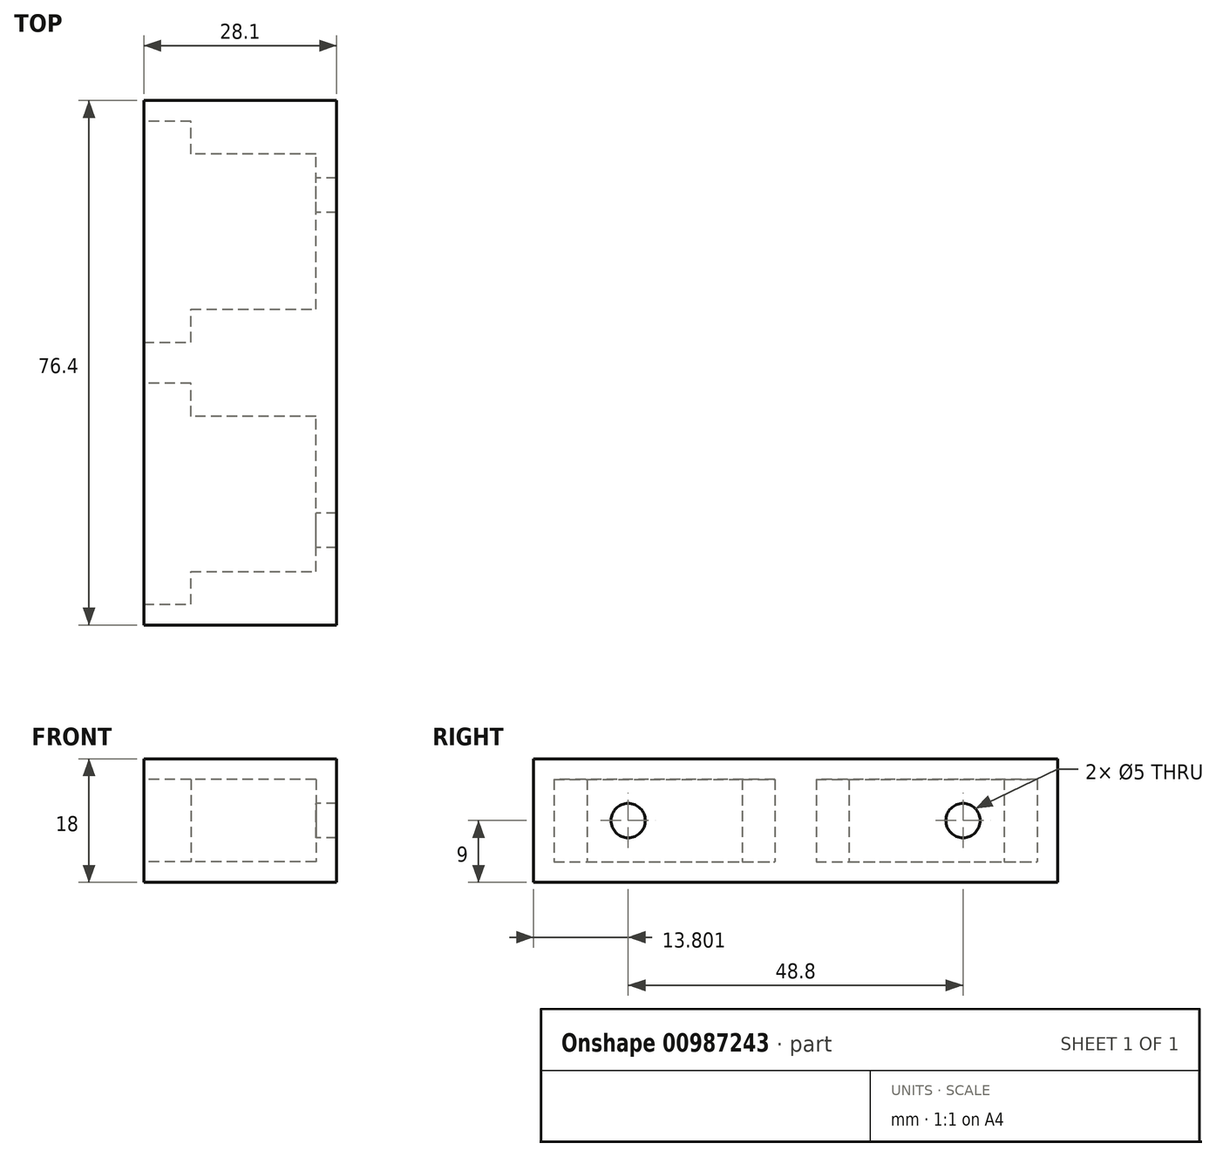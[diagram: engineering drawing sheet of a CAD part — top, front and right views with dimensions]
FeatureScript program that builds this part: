
annotation { "Feature Type Name" : "Feature", "Feature Type Description" : "" }
export const myFeature = defineFeature(function(context is Context, id is Id, definition is map)
    precondition{}
    {
        {
            assignVariable(context, id + "F0", {"name" : "ServoF", "anyValue" : 12});
        }
        {
            var Q0;
            Q0=qCreatedBy(makeId("Top.planeOp"),FACE);
            var sketch = newSketch(context, id + "F1", { "sketchPlane" : qUnion([Q0])});
            skLineSegment(sketch, "E0", {"start": v(-63.12, 39.48) * mm, "end": v(-35.02, 39.48) * mm});
            skLineSegment(sketch, "E1", {"start": v(-35.02, 39.48) * mm, "end": v(-35.02, -36.92) * mm});
            skLineSegment(sketch, "E2", {"start": v(-35.02, -36.92) * mm, "end": v(-63.12, -36.92) * mm});
            skLineSegment(sketch, "E3", {"start": v(-63.12, -36.92) * mm, "end": v(-63.12, -33.92) * mm});
            skLineSegment(sketch, "E4", {"start": v(-63.12, -33.92) * mm, "end": v(-56.27, -33.92) * mm});
            skLineSegment(sketch, "E5", {"start": v(-56.27, -33.92) * mm, "end": v(-56.27, -29.12) * mm});
            skLineSegment(sketch, "E6", {"start": v(-56.27, -29.12) * mm, "end": v(-38.02, -29.12) * mm});
            skLineSegment(sketch, "E7", {"start": v(-38.02, -29.12) * mm, "end": v(-38.02, -6.52) * mm});
            skLineSegment(sketch, "E8", {"start": v(-38.02, -6.52) * mm, "end": v(-56.27, -6.52) * mm});
            skLineSegment(sketch, "E9", {"start": v(-56.27, -6.52) * mm, "end": v(-56.27, -1.72) * mm});
            skLineSegment(sketch, "E10", {"start": v(-56.27, -1.72) * mm, "end": v(-63.12, -1.72) * mm});
            skLineSegment(sketch, "E11", {"start": v(-63.12, -1.72) * mm, "end": v(-63.12, 4.28) * mm});
            skLineSegment(sketch, "E12", {"start": v(-63.12, 4.28) * mm, "end": v(-56.27, 4.28) * mm});
            skLineSegment(sketch, "E13", {"start": v(-56.27, 4.28) * mm, "end": v(-56.27, 9.08) * mm});
            skLineSegment(sketch, "E14", {"start": v(-56.27, 9.08) * mm, "end": v(-38.02, 9.08) * mm});
            skLineSegment(sketch, "E15", {"start": v(-38.02, 9.08) * mm, "end": v(-38.02, 31.68) * mm});
            skLineSegment(sketch, "E16", {"start": v(-38.02, 31.68) * mm, "end": v(-56.27, 31.68) * mm});
            skLineSegment(sketch, "E17", {"start": v(-56.27, 31.68) * mm, "end": v(-56.27, 36.48) * mm});
            skLineSegment(sketch, "E18", {"start": v(-56.27, 36.48) * mm, "end": v(-63.12, 36.48) * mm});
            skLineSegment(sketch, "E19", {"start": v(-63.12, 36.48) * mm, "end": v(-63.12, 39.48) * mm});
            skSolve(sketch);
        }
        {
            var Q0;
            Q0=qSketchRegion(id+"F1",true);
            extrude(context, id + "F2", {"entities" : qUnion([Q0]), "depth" : (getVariable(context, 'ServoF')) * mm, "offsetDistance" : 25 * mm});
        }
        {
            var Q0;
            Q0=makeQuery(id+"F2.opExtrude","CAP_FACE",FACE,{"disambiguationData":[OSD([sQuery(id+"F1.wireOp",EDGE,"E0"),sQuery(id+"F1.wireOp",EDGE,"E1"),sQuery(id+"F1.wireOp",EDGE,"E2"),sQuery(id+"F1.wireOp",EDGE,"E3"),sQuery(id+"F1.wireOp",EDGE,"E4"),sQuery(id+"F1.wireOp",EDGE,"E5"),sQuery(id+"F1.wireOp",EDGE,"E6"),sQuery(id+"F1.wireOp",EDGE,"E7"),sQuery(id+"F1.wireOp",EDGE,"E8"),sQuery(id+"F1.wireOp",EDGE,"E9"),sQuery(id+"F1.wireOp",EDGE,"E10"),sQuery(id+"F1.wireOp",EDGE,"E11"),sQuery(id+"F1.wireOp",EDGE,"E12"),sQuery(id+"F1.wireOp",EDGE,"E13"),sQuery(id+"F1.wireOp",EDGE,"E14"),sQuery(id+"F1.wireOp",EDGE,"E15"),sQuery(id+"F1.wireOp",EDGE,"E16"),sQuery(id+"F1.wireOp",EDGE,"E17"),sQuery(id+"F1.wireOp",EDGE,"E18"),sQuery(id+"F1.wireOp",EDGE,"E19")])],"isStart":false});
            var sketch = newSketch(context, id + "F3", { "sketchPlane" : qUnion([Q0])});
            skLineSegment(sketch, "E20.bottom", {"start": v(-63.12, -36.92) * mm, "end": v(-35.02, -36.92) * mm});
            skLineSegment(sketch, "E20.top", {"start": v(-63.12, 39.48) * mm, "end": v(-35.02, 39.48) * mm});
            skLineSegment(sketch, "E20.left", {"start": v(-63.12, 39.48) * mm, "end": v(-63.12, -36.92) * mm});
            skLineSegment(sketch, "E20.right", {"start": v(-35.02, 39.48) * mm, "end": v(-35.02, -36.92) * mm});
            skSolve(sketch);
        }
        {
            var Q0;
            Q0=makeQuery(id+"F2.opExtrude","CAP_FACE",FACE,{"disambiguationData":[OSD([sQuery(id+"F1.wireOp",EDGE,"E0"),sQuery(id+"F1.wireOp",EDGE,"E1"),sQuery(id+"F1.wireOp",EDGE,"E2"),sQuery(id+"F1.wireOp",EDGE,"E3"),sQuery(id+"F1.wireOp",EDGE,"E4"),sQuery(id+"F1.wireOp",EDGE,"E5"),sQuery(id+"F1.wireOp",EDGE,"E6"),sQuery(id+"F1.wireOp",EDGE,"E7"),sQuery(id+"F1.wireOp",EDGE,"E8"),sQuery(id+"F1.wireOp",EDGE,"E9"),sQuery(id+"F1.wireOp",EDGE,"E10"),sQuery(id+"F1.wireOp",EDGE,"E11"),sQuery(id+"F1.wireOp",EDGE,"E12"),sQuery(id+"F1.wireOp",EDGE,"E13"),sQuery(id+"F1.wireOp",EDGE,"E14"),sQuery(id+"F1.wireOp",EDGE,"E15"),sQuery(id+"F1.wireOp",EDGE,"E16"),sQuery(id+"F1.wireOp",EDGE,"E17"),sQuery(id+"F1.wireOp",EDGE,"E18"),sQuery(id+"F1.wireOp",EDGE,"E19")])],"isStart":true});
            var sketch = newSketch(context, id + "F4", { "sketchPlane" : qUnion([Q0])});
            skLineSegment(sketch, "E21.bottom", {"start": v(-63.12, -39.48) * mm, "end": v(-35.02, -39.48) * mm});
            skLineSegment(sketch, "E21.top", {"start": v(-63.12, 36.92) * mm, "end": v(-35.02, 36.92) * mm});
            skLineSegment(sketch, "E21.left", {"start": v(-63.12, 36.92) * mm, "end": v(-63.12, -39.48) * mm});
            skLineSegment(sketch, "E21.right", {"start": v(-35.02, 36.92) * mm, "end": v(-35.02, -39.48) * mm});
            skSolve(sketch);
        }
        {
            var Q0;
            Q0=makeQuery(id+"F2.opExtrude","SWEPT_FACE",FACE,{"disambiguationData":[OSD([sQuery(id+"F1.wireOp",EDGE,"E15")])]});
            var sketch = newSketch(context, id + "F5", { "sketchPlane" : qUnion([Q0])});
            skCircle(sketch, "E22", {"center": v(-25.68, 6) * mm, "radius": 2.5 * mm});
            skCircle(sketch, "E23", {"center": v(0, 0) * mm, "radius": 2.5 * mm});
            skSolve(sketch);
        }
        {
            var Q0;
            Q0=makeQuery(id+"F2.opExtrude","SWEPT_FACE",FACE,{"disambiguationData":[OSD([sQuery(id+"F1.wireOp",EDGE,"E7")])]});
            var sketch = newSketch(context, id + "F6", { "sketchPlane" : qUnion([Q0])});
            skCircle(sketch, "E24", {"center": v(23.12, 6) * mm, "radius": 2.5 * mm});
            skSolve(sketch);
        }
        {
            var Q0;
            Q0=qSketchRegion(id+"F3",true);
            extrude(context, id + "F7", {"entities" : qUnion([Q0]), "operationType" : NewBodyOperationType.ADD, "depth" : 3 * mm, "offsetDistance" : 25 * mm});
        }
        {
            var Q0;
            Q0=qSketchRegion(id+"F4",true);
            extrude(context, id + "F8", {"entities" : qUnion([Q0]), "operationType" : NewBodyOperationType.ADD, "depth" : 3 * mm, "offsetDistance" : 25 * mm});
        }
        {
            var Q0;
            Q0=sQuery(id+"F5.wireOp",VERTEX,"E22.center");
            var Q1;
            Q1=makeQuery(id+"F2.opExtrude","SWEPT_BODY",BODY,{"disambiguationData":[OSD([sQuery(id+"F1.wireOp",EDGE,"E0"),sQuery(id+"F1.wireOp",EDGE,"E1"),sQuery(id+"F1.wireOp",EDGE,"E2"),sQuery(id+"F1.wireOp",EDGE,"E3"),sQuery(id+"F1.wireOp",EDGE,"E4"),sQuery(id+"F1.wireOp",EDGE,"E5"),sQuery(id+"F1.wireOp",EDGE,"E6"),sQuery(id+"F1.wireOp",EDGE,"E7"),sQuery(id+"F1.wireOp",EDGE,"E8"),sQuery(id+"F1.wireOp",EDGE,"E9"),sQuery(id+"F1.wireOp",EDGE,"E10"),sQuery(id+"F1.wireOp",EDGE,"E11"),sQuery(id+"F1.wireOp",EDGE,"E12"),sQuery(id+"F1.wireOp",EDGE,"E13"),sQuery(id+"F1.wireOp",EDGE,"E14"),sQuery(id+"F1.wireOp",EDGE,"E15"),sQuery(id+"F1.wireOp",EDGE,"E16"),sQuery(id+"F1.wireOp",EDGE,"E17"),sQuery(id+"F1.wireOp",EDGE,"E18"),sQuery(id+"F1.wireOp",EDGE,"E19")])]});
            hole(context, id + "F9", {"style" : HoleStyle.SIMPLE, "endStyle" : HoleEndStyle.THROUGH, "holeDiameter" : 5 * mm, "majorDiameter" : 5 * mm, "isTappedThrough" : true, "tappedDepth" : 12 * mm, "tapClearance" : 3, "locations" : qUnion([Q0]), "scope" : qUnion([Q1])});
        }
        {
            var Q0;
            Q0=sQuery(id+"F6.wireOp",VERTEX,"E24.center");
            var Q1;
            Q1=makeQuery(id+"F2.opExtrude","SWEPT_BODY",BODY,{"disambiguationData":[OSD([sQuery(id+"F1.wireOp",EDGE,"E0"),sQuery(id+"F1.wireOp",EDGE,"E1"),sQuery(id+"F1.wireOp",EDGE,"E2"),sQuery(id+"F1.wireOp",EDGE,"E3"),sQuery(id+"F1.wireOp",EDGE,"E4"),sQuery(id+"F1.wireOp",EDGE,"E5"),sQuery(id+"F1.wireOp",EDGE,"E6"),sQuery(id+"F1.wireOp",EDGE,"E7"),sQuery(id+"F1.wireOp",EDGE,"E8"),sQuery(id+"F1.wireOp",EDGE,"E9"),sQuery(id+"F1.wireOp",EDGE,"E10"),sQuery(id+"F1.wireOp",EDGE,"E11"),sQuery(id+"F1.wireOp",EDGE,"E12"),sQuery(id+"F1.wireOp",EDGE,"E13"),sQuery(id+"F1.wireOp",EDGE,"E14"),sQuery(id+"F1.wireOp",EDGE,"E15"),sQuery(id+"F1.wireOp",EDGE,"E16"),sQuery(id+"F1.wireOp",EDGE,"E17"),sQuery(id+"F1.wireOp",EDGE,"E18"),sQuery(id+"F1.wireOp",EDGE,"E19")])]});
            hole(context, id + "F10", {"style" : HoleStyle.SIMPLE, "endStyle" : HoleEndStyle.THROUGH, "holeDiameter" : 5 * mm, "majorDiameter" : 5 * mm, "isTappedThrough" : true, "tappedDepth" : 12 * mm, "tapClearance" : 3, "locations" : qUnion([Q0]), "scope" : qUnion([Q1])});
        }
    });
